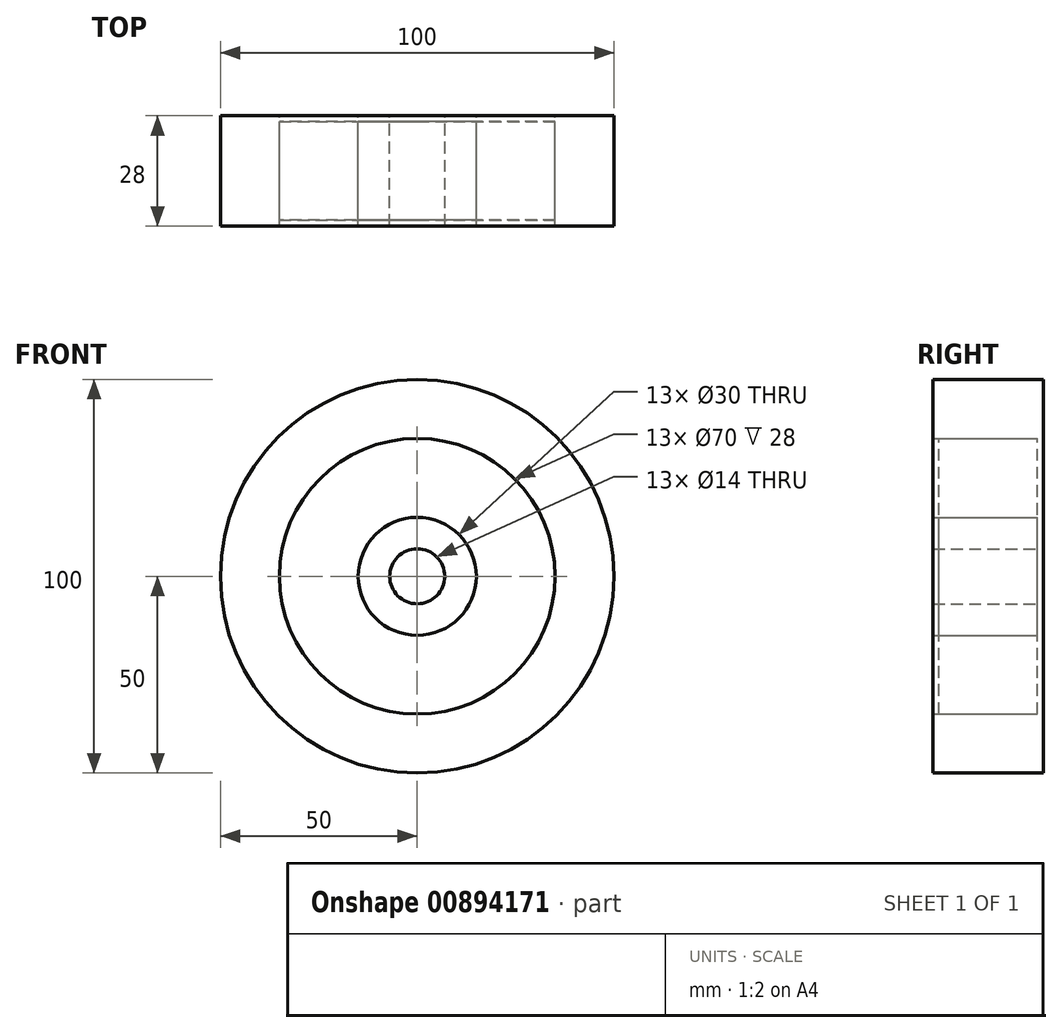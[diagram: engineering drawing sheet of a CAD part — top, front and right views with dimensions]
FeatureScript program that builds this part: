
annotation { "Feature Type Name" : "Feature", "Feature Type Description" : "" }
export const myFeature = defineFeature(function(context is Context, id is Id, definition is map)
    precondition{}
    {
        {
            var Q0;
            Q0=qCreatedBy(makeId("Front.planeOp"),FACE);
            var sketch = newSketch(context, id + "F0", { "sketchPlane" : qUnion([Q0])});
            skCircle(sketch, "E0", {"center": v(0, 0) * mm, "radius": 35 * mm});
            skCircle(sketch, "E1", {"center": v(0, 0) * mm, "radius": 15 * mm});
            skCircle(sketch, "E2", {"center": v(0, 0) * mm, "radius": 50 * mm});
            skCircle(sketch, "E3", {"center": v(0, 0) * mm, "radius": 7 * mm});
            skSolve(sketch);
        }
        {
            var Q0;
            Q0 = qSketchRegion(id + "F0", true);
            var Q1;
            Q1=makeQuery(id+"F0.imprint","IMPRINT",FACE,{"disambiguationData":[TD([[makeQuery(id+"F0.imprint","IMPRINT",EDGE,{"derivedFrom":sQuery(id+"F0.wireOp",EDGE,"E1")}),1.0]])]});
            extrude(context, id + "F1", {"entities" : qUnion([Q0, Q1]), "endBound" : BoundingType.SYMMETRIC, "depth" : 28 * mm, "offsetDistance" : 25 * mm});
        }
        {
            var Q0;
            Q0=makeQuery(id+"F0.imprint","IMPRINT",FACE,{"disambiguationData":[TD([[makeQuery(id+"F0.imprint","IMPRINT",EDGE,{"derivedFrom":sQuery(id+"F0.wireOp",EDGE,"E0")}),1.0]])]});
            extrude(context, id + "F2", {"entities" : qUnion([Q0]), "endBound" : BoundingType.SYMMETRIC, "depth" : 25 * mm, "offsetDistance" : 25 * mm});
        }
    });
